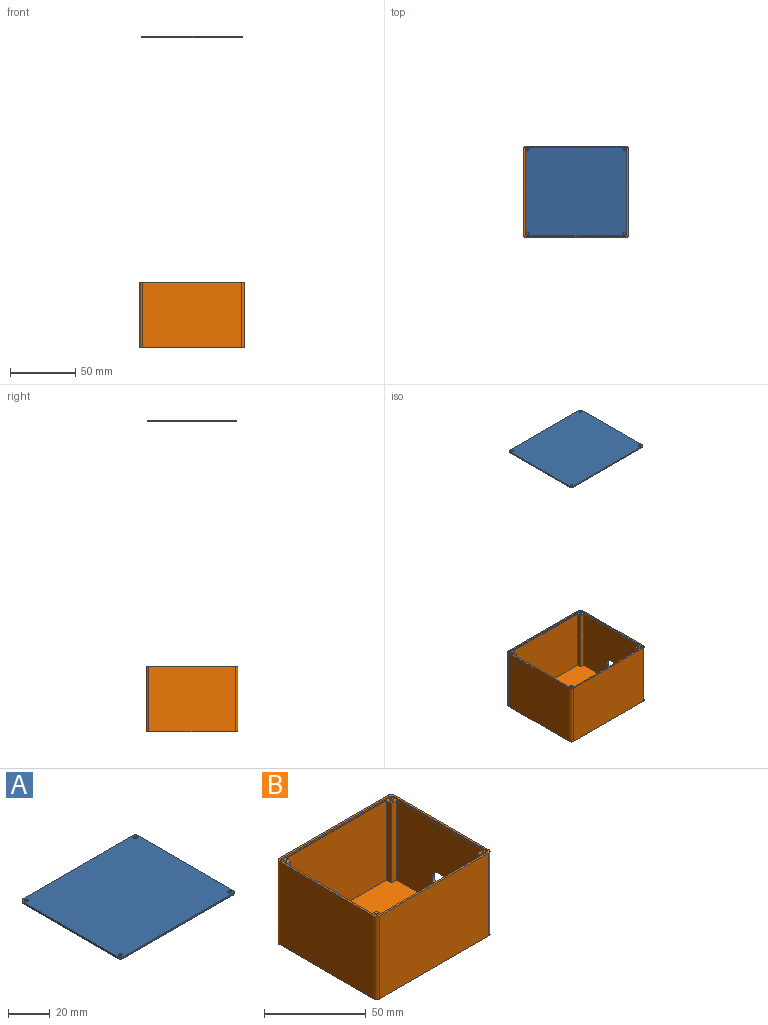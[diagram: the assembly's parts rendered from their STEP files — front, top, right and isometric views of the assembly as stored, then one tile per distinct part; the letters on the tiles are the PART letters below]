
ASSEMBLY  parts=2 mates=1
PART A: 14 faces, bbox 78x68x1 mm
  f0: plane 74x1mm, normal (0,1,0), area 74mm2, adj f4,f5,f10,f13
  f1: plane 64x1mm, normal (-1,0,0), area 64mm2, adj f4,f5,f10,f11
  f2: plane 74x1mm, normal (0,-1,0), area 74mm2, adj f4,f5,f11,f12
  f3: plane 64x1mm, normal (1,0,0), area 64mm2, adj f4,f5,f12,f13
  f4: plane 78x68mm, normal (0,0,1), area 5288mm2, adj f0,f1,f2,f3,f6,f7,f8,f9
  f5: plane 78x68mm, normal (0,0,-1), area 5288mm2, adj f0,f1,f2,f3,f6,f7,f8,f9
  f6: cylinder r=1mm len=2mm, axis (0,0,1), area 6.3mm2, adj f4,f5
  f7: cylinder r=1mm len=2mm, axis (0,0,1), area 6.3mm2, adj f4,f5
  f8: cylinder r=1mm len=2mm, axis (0,0,1), area 6.3mm2, adj f4,f5
  f9: cylinder r=1mm len=2mm, axis (0,0,1), area 6.3mm2, adj f4,f5
  f10: cylinder r=2mm len=2mm, axis (0,0,1), area 3.1mm2, adj f0,f1,f4,f5
  f11: cylinder r=2mm len=2mm, axis (0,0,-1), area 3.1mm2, adj f1,f2,f4,f5
  f12: cylinder r=2mm len=2mm, axis (0,0,1), area 3.1mm2, adj f2,f3,f4,f5
  f13: cylinder r=2mm len=2mm, axis (0,0,-1), area 3.1mm2, adj f0,f3,f4,f5
PART B: 91 faces, bbox 80x70x50 mm
  f0: cylinder r=1mm len=5mm, axis (0,0,1), area 31.4mm2, adj f53,f84
  f1: cylinder r=1mm len=5mm, axis (0,0,1), area 31.4mm2, adj f52,f77
  f2: cylinder r=1mm len=5mm, axis (0,0,1), area 31.4mm2, adj f54,f70
  f3: cylinder r=1mm len=5mm, axis (0,0,1), area 31.4mm2, adj f51,f63
  f4: cylinder r=2mm len=4mm, axis (0,0,-1), area 50.3mm2, adj f51,f62
  f5: cylinder r=2mm len=4mm, axis (0,0,-1), area 50.3mm2, adj f53,f60
  f6: cylinder r=2mm len=4mm, axis (0,0,-1), area 50.3mm2, adj f54,f58
  f7: cylinder r=2mm len=4mm, axis (0,0,-1), area 50.3mm2, adj f52,f56
  f8: plane 60x48mm, normal (-1,0,0), area 2801.5mm2, adj f10,f23,f27,f30,f50
  f9: plane 70x48mm, normal (0,1,0), area 3360mm2, adj f10,f23,f28,f31
  f10: plane 77x67mm, normal (0,0,1), area 4908.5mm2, adj f8,f9,f11,f12,f24,f25,f26,f27
  f11: plane 59x48mm, normal (1,0,0), area 2832mm2, adj f10,f23,f29,f44
  f12: plane 69x48mm, normal (0,-1,0), area 3312mm2, adj f10,f23,f26,f45
  f13: plane 74x1mm, normal (0,-1,0), area 74mm2, adj f17,f23,f46,f49
  f14: plane 64x1mm, normal (1,0,0), area 64mm2, adj f17,f23,f46,f47
  f15: plane 74x1mm, normal (0,1,0), area 74mm2, adj f17,f23,f47,f48
  f16: plane 64x1mm, normal (-1,0,0), area 64mm2, adj f17,f23,f48,f49
  f17: plane 80x70mm, normal (0,0,1), area 296mm2, adj f13,f14,f15,f16,f18,f19,f20,f21
  f18: plane 76x50mm, normal (0,1,0), area 3800mm2, adj f17,f22,f42,f43
  f19: plane 66x50mm, normal (-1,0,0), area 3300mm2, adj f17,f22,f41,f43
  f20: plane 76x50mm, normal (0,-1,0), area 3800mm2, adj f17,f22,f40,f41
  f21: plane 66x50mm, normal (1,0,0), area 3221.5mm2, adj f17,f22,f40,f42,f50
  f22: plane 80x70mm, normal (0,0,-1), area 5503mm2, adj f18,f19,f20,f21,f40,f41,f42,f43
  f23: plane 78x68mm, normal (0,0,1), area 178.4mm2, adj f8,f9,f11,f12,f13,f14,f15,f16
  f24: plane 48x2.5mm, normal (0,-1,0), area 120mm2, adj f10,f23,f25,f44
  f25: plane 48x2.5mm, normal (1,0,0), area 120mm2, adj f10,f23,f24,f45
  f26: plane 48x3.5mm, normal (-1,0,0), area 168mm2, adj f10,f12,f23,f27
  f27: plane 48x3.5mm, normal (0,-1,0), area 168mm2, adj f8,f10,f23,f26
  f28: plane 48x3.5mm, normal (1,0,0), area 168mm2, adj f9,f10,f23,f29
  f29: plane 48x3.5mm, normal (0,1,0), area 168mm2, adj f10,f11,f23,f28
  f30: plane 48x3.5mm, normal (0,1,0), area 168mm2, adj f8,f10,f23,f31
  f31: plane 48x3.5mm, normal (-1,0,0), area 168mm2, adj f9,f10,f23,f30
  f32: cylinder r=1mm len=15mm, axis (0,0,1), area 94.2mm2, adj f23,f33
  f33: plane 2x2mm, normal (0,0,1), area 3.1mm2, adj f32
  f34: cylinder r=1mm len=15mm, axis (0,0,1), area 94.2mm2, adj f23,f35
  f35: plane 2x2mm, normal (0,0,1), area 3.1mm2, adj f34
  f36: cylinder r=1mm len=15mm, axis (0,0,1), area 94.2mm2, adj f23,f37
  f37: plane 2x2mm, normal (0,0,1), area 3.1mm2, adj f36
  f38: cylinder r=1mm len=15mm, axis (0,0,1), area 94.2mm2, adj f23,f39
  f39: plane 2x2mm, normal (0,0,1), area 3.1mm2, adj f38
  f40: cylinder r=2mm len=50mm, axis (0,0,1), area 157.1mm2, adj f17,f20,f21,f22
  f41: cylinder r=2mm len=50mm, axis (0,0,-1), area 157.1mm2, adj f17,f19,f20,f22
  f42: cylinder r=2mm len=50mm, axis (0,0,-1), area 157.1mm2, adj f17,f18,f21,f22
  f43: cylinder r=2mm len=50mm, axis (0,0,1), area 157.1mm2, adj f17,f18,f19,f22
  f44: cylinder r=1mm len=48mm, axis (0,0,-1), area 75.4mm2, adj f10,f11,f23,f24
  f45: cylinder r=1mm len=48mm, axis (0,0,-1), area 75.4mm2, adj f10,f12,f23,f25
  f46: cylinder r=2mm len=2mm, axis (0,0,1), area 3.1mm2, adj f13,f14,f17,f23
  f47: cylinder r=2mm len=2mm, axis (0,0,-1), area 3.1mm2, adj f14,f15,f17,f23
  f48: cylinder r=2mm len=2mm, axis (0,0,1), area 3.1mm2, adj f15,f16,f17,f23
  f49: cylinder r=2mm len=2mm, axis (0,0,-1), area 3.1mm2, adj f13,f16,f17,f23
  f50: cylinder r=5mm len=10mm, axis (1,0,0), area 47.1mm2, adj f8,f21
  f51: plane 4x4mm, normal (0,0,1), area 9.4mm2, adj f3,f4
  f52: plane 4x4mm, normal (0,0,1), area 9.4mm2, adj f1,f7
  f53: plane 4x4mm, normal (0,0,1), area 9.4mm2, adj f0,f5
  f54: plane 4x4mm, normal (0,0,1), area 9.4mm2, adj f2,f6
  f55: cylinder r=4mm len=8mm, axis (0,0,-1), area 50.3mm2, adj f10,f56
  f56: plane 8x8mm, normal (0,0,1), area 37.7mm2, adj f7,f55
  f57: cylinder r=4mm len=8mm, axis (0,0,-1), area 50.3mm2, adj f10,f58
  f58: plane 8x8mm, normal (0,0,1), area 37.7mm2, adj f6,f57
  f59: cylinder r=4mm len=8mm, axis (0,0,-1), area 50.3mm2, adj f10,f60
  f60: plane 8x8mm, normal (0,0,1), area 37.7mm2, adj f5,f59
  f61: cylinder r=4mm len=8mm, axis (0,0,-1), area 50.3mm2, adj f10,f62
  f62: plane 8x8mm, normal (0,0,1), area 37.7mm2, adj f4,f61
  f63: plane 6x5.2mm, normal (0,0,-1), area 20.2mm2, adj f3,f64,f65,f66,f67,f68,f69
  f64: plane 2.6x2mm, normal (-0.5,-0.87,0), area 6mm2, adj f22,f63,f65,f69
  f65: plane 3x2mm, normal (-1,0,0), area 6mm2, adj f22,f63,f64,f66
  f66: plane 2.6x2mm, normal (-0.5,0.87,0), area 6mm2, adj f22,f63,f65,f67
  f67: plane 2.6x2mm, normal (0.5,0.87,0), area 6mm2, adj f22,f63,f66,f68
  f68: plane 3x2mm, normal (1,0,0), area 6mm2, adj f22,f63,f67,f69
  f69: plane 2.6x2mm, normal (0.5,-0.87,0), area 6mm2, adj f22,f63,f64,f68
  f70: plane 6x5.2mm, normal (0,0,-1), area 20.2mm2, adj f2,f71,f72,f73,f74,f75,f76
  f71: plane 2.6x2mm, normal (-0.5,-0.87,0), area 6mm2, adj f22,f70,f72,f76
  f72: plane 3x2mm, normal (-1,0,0), area 6mm2, adj f22,f70,f71,f73
  f73: plane 2.6x2mm, normal (-0.5,0.87,0), area 6mm2, adj f22,f70,f72,f74
  f74: plane 2.6x2mm, normal (0.5,0.87,0), area 6mm2, adj f22,f70,f73,f75
  f75: plane 3x2mm, normal (1,0,0), area 6mm2, adj f22,f70,f74,f76
  f76: plane 2.6x2mm, normal (0.5,-0.87,0), area 6mm2, adj f22,f70,f71,f75
  f77: plane 6x5.2mm, normal (0,0,-1), area 20.2mm2, adj f1,f78,f79,f80,f81,f82,f83
  f78: plane 2.6x2mm, normal (-0.5,-0.87,0), area 6mm2, adj f22,f77,f79,f83
  f79: plane 3x2mm, normal (-1,0,0), area 6mm2, adj f22,f77,f78,f80
  f80: plane 2.6x2mm, normal (-0.5,0.87,0), area 6mm2, adj f22,f77,f79,f81
  f81: plane 2.6x2mm, normal (0.5,0.87,0), area 6mm2, adj f22,f77,f80,f82
  f82: plane 3x2mm, normal (1,0,0), area 6mm2, adj f22,f77,f81,f83
  f83: plane 2.6x2mm, normal (0.5,-0.87,0), area 6mm2, adj f22,f77,f78,f82
  f84: plane 6x5.2mm, normal (0,0,-1), area 20.2mm2, adj f0,f85,f86,f87,f88,f89,f90
  f85: plane 2.6x2mm, normal (-0.5,-0.87,0), area 6mm2, adj f22,f84,f86,f90
  f86: plane 3x2mm, normal (-1,0,0), area 6mm2, adj f22,f84,f85,f87
  f87: plane 2.6x2mm, normal (-0.5,0.87,0), area 6mm2, adj f22,f84,f86,f88
  f88: plane 2.6x2mm, normal (0.5,0.87,0), area 6mm2, adj f22,f84,f87,f89
  f89: plane 3x2mm, normal (1,0,0), area 6mm2, adj f22,f84,f88,f90
  f90: plane 2.6x2mm, normal (0.5,-0.87,0), area 6mm2, adj f22,f84,f85,f89
PLACE A t=(2.43,-85.76,237.68)mm
PLACE B at identity fixed
MATE slider B.f38 <-> A.f9  axis (0,0,1) through (3,-67,49)mm
